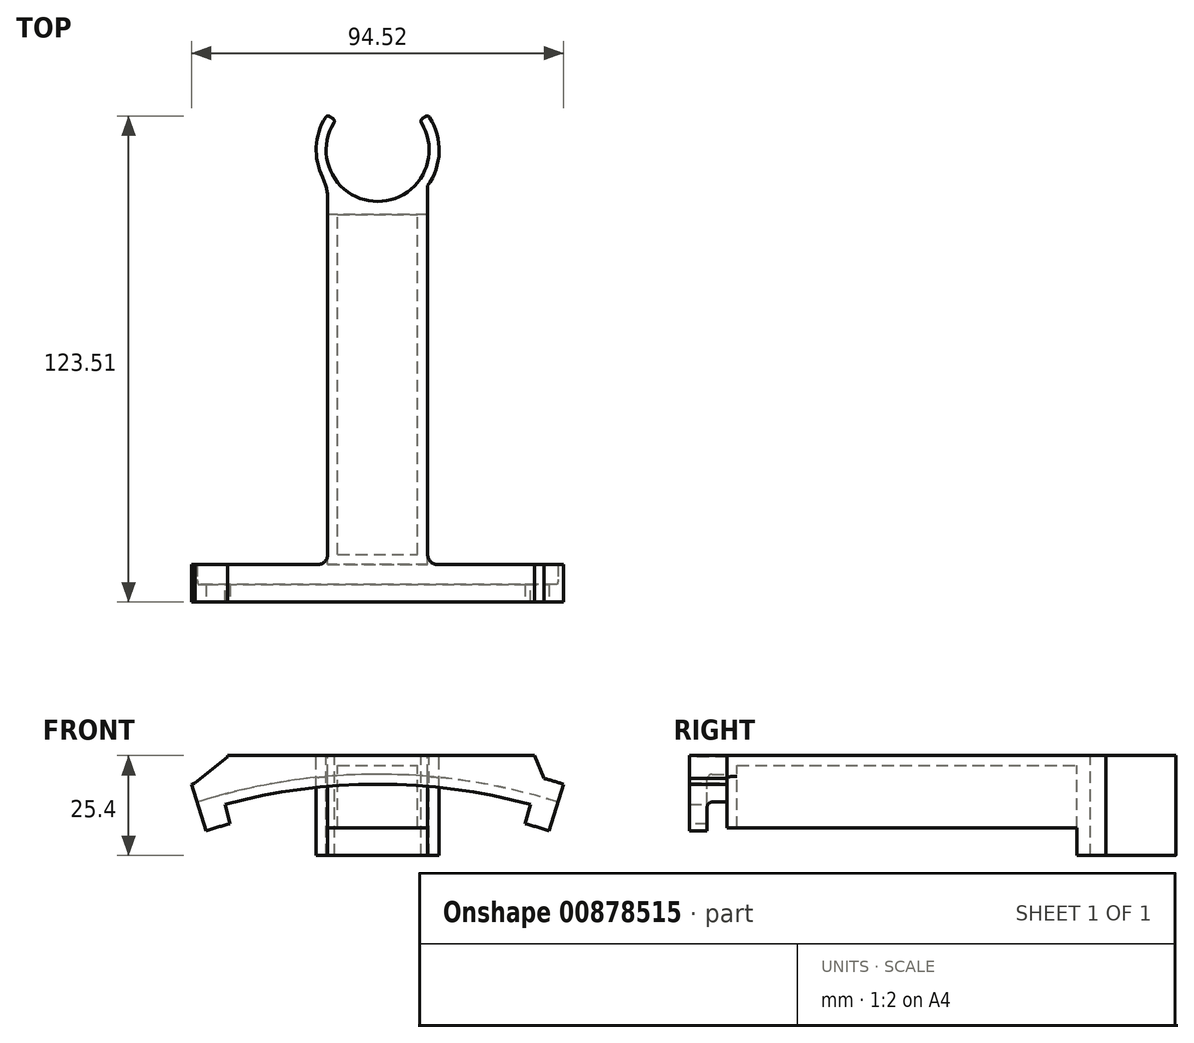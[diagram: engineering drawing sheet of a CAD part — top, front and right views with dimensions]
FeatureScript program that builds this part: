
annotation { "Feature Type Name" : "Feature", "Feature Type Description" : "" }
export const myFeature = defineFeature(function(context is Context, id is Id, definition is map)
    precondition{}
    {
        {
            var Q0;
            Q0=qCreatedBy(makeId("Top.planeOp"),FACE);
            var sketch = newSketch(context, id + "F0", { "sketchPlane" : qUnion([Q0])});
            skCircle(sketch, "E0", {"center": v(0, 0) * mm, "radius": 15.62 * mm});
            skCircle(sketch, "E1", {"center": v(0, 0) * mm, "radius": 13.08 * mm});
            skLineSegment(sketch, "E2", {"start": v(-53.94, 0) * mm, "end": v(51.47, 0) * mm, "construction": true});
            skLineSegment(sketch, "E3", {"start": v(0, 37.95) * mm, "end": v(0, -48.77) * mm, "construction": true});
            skLineSegment(sketch, "E4", {"start": v(0, 0) * mm, "end": v(-12.8, 8.96) * mm});
            skLineSegment(sketch, "E5.MirrorCS", {"start": v(0, 0) * mm, "end": v(12.8, 8.96) * mm});
            skLineSegment(sketch, "E6.top", {"start": v(-12.7, -16.43) * mm, "end": v(12.7, -16.43) * mm});
            skLineSegment(sketch, "E6.left", {"start": v(-12.7, -9.1) * mm, "end": v(-12.7, -16.43) * mm});
            skLineSegment(sketch, "E6.right", {"start": v(12.7, -9.1) * mm, "end": v(12.7, -16.43) * mm});
            skPoint(sketch, "E6.middle", {"position": v(0, -12.76) * mm});
            skCircle(sketch, "E7", {"center": v(0, 0) * mm, "radius": 13.34 * mm, "construction": true});
            skSolve(sketch);
        }
        {
            var Q0;
            {var subQ0=sQuery(id+"F0.wireOp",EDGE,"E4");var subQ5=sQuery(id+"F0.wireOp",EDGE,"E0");var subQ9=makeQuery(id+"F0.imprint","INTERSECT",VERTEX,{"derivedFrom":[subQ5,subQ0]});Q0=makeQuery(id+"F0.imprint","IMPRINT",FACE,{"disambiguationData":[TD([[makeQuery(id+"F0.imprint","IMPRINT",EDGE,{"disambiguationData":[TD([[subQ9,-1.0]])],"derivedFrom":subQ5}),1.0]])]});}
            extrude(context, id + "F1", {"entities" : qUnion([Q0]), "oppositeDirection" : true, "depth" : 25.4 * mm, "offsetDistance" : 25.4 * mm});
        }
        {
            var Q0;
            Q0=makeQuery(id+"F0.imprint","IMPRINT",FACE,{"disambiguationData":[TD([[makeQuery(id+"F0.imprint","IMPRINT",EDGE,{"derivedFrom":sQuery(id+"F0.wireOp",EDGE,"E6.top")}),1.0]])]});
            var Q1;
            Q1=makeQuery(id+"F1.opExtrude","CAP_FACE",FACE,{"disambiguationData":[OSD([sQuery(id+"F0.wireOp",EDGE,"E0"),sQuery(id+"F0.wireOp",EDGE,"E1"),sQuery(id+"F0.wireOp",EDGE,"E4"),sQuery(id+"F0.wireOp",EDGE,"E5.MirrorCS")])],"isStart":false});
            extrude(context, id + "F2", {"entities" : qUnion([Q0]), "operationType" : NewBodyOperationType.ADD, "endBound" : BoundingType.UP_TO_SURFACE, "oppositeDirection" : true, "depth" : 19.05 * mm, "endBoundEntityFace" : qUnion([Q1]), "offsetDistance" : 25.4 * mm});
        }
        {
            var Q0;
            Q0=makeQuery(id+"F2.opExtrude","SWEPT_EDGE",EDGE,{"disambiguationData":[OSD([sQuery(id+"F0.wireOp",EDGE,"E0"),sQuery(id+"F0.wireOp",EDGE,"E6.left")])]});
            var Q1;
            Q1=makeQuery(id+"F2.opExtrude","SWEPT_EDGE",EDGE,{"disambiguationData":[OSD([sQuery(id+"F0.wireOp",EDGE,"E0"),sQuery(id+"F0.wireOp",EDGE,"E6.right")])]});
            fillet(context, id + "F3", {"entities" : qUnion([Q0, Q1]), "radius" : 12.7 * mm, "tangentPropagation" : true, "allowEdgeOverflow" : false});
        }
        {
            var Q0;
            Q0=makeQuery(id+"F1.opExtrude","SWEPT_EDGE",EDGE,{"disambiguationData":[OSD([sQuery(id+"F0.wireOp",EDGE,"E0"),sQuery(id+"F0.wireOp",EDGE,"E4")])]});
            var Q1;
            Q1=makeQuery(id+"F1.opExtrude","SWEPT_EDGE",EDGE,{"disambiguationData":[OSD([sQuery(id+"F0.wireOp",EDGE,"E1"),sQuery(id+"F0.wireOp",EDGE,"E4")])]});
            var Q2;
            Q2=makeQuery(id+"F1.opExtrude","SWEPT_EDGE",EDGE,{"disambiguationData":[OSD([sQuery(id+"F0.wireOp",EDGE,"E0"),sQuery(id+"F0.wireOp",EDGE,"E5.MirrorCS")])]});
            var Q3;
            Q3=makeQuery(id+"F1.opExtrude","SWEPT_EDGE",EDGE,{"disambiguationData":[OSD([sQuery(id+"F0.wireOp",EDGE,"E1"),sQuery(id+"F0.wireOp",EDGE,"E5.MirrorCS")])]});
            fillet(context, id + "F4", {"entities" : qUnion([Q0, Q1, Q2, Q3]), "radius" : 0.76 * mm, "tangentPropagation" : true, "allowEdgeOverflow" : false});
        }
        {
            var Q0;
            Q0=makeQuery(id+"F2.opExtrude","SWEPT_FACE",FACE,{"disambiguationData":[OSD([sQuery(id+"F0.wireOp",EDGE,"E6.top")])]});
            var sketch = newSketch(context, id + "F5", { "sketchPlane" : qUnion([Q0])});
            skLineSegment(sketch, "E8.0", {"start": v(12.7, -25.4) * mm, "end": v(12.7, 0) * mm});
            skLineSegment(sketch, "E8.1", {"start": v(-12.7, 0) * mm, "end": v(12.7, 0) * mm});
            skLineSegment(sketch, "E8.2", {"start": v(-12.7, -25.4) * mm, "end": v(-12.7, 0) * mm});
            skLineSegment(sketch, "E9.0", {"start": v(-10.16, -25.4) * mm, "end": v(-10.16, -2.54) * mm});
            skLineSegment(sketch, "E9.1", {"start": v(-10.16, -2.54) * mm, "end": v(10.16, -2.54) * mm});
            skLineSegment(sketch, "E9.2", {"start": v(10.16, -25.4) * mm, "end": v(10.16, -2.54) * mm});
            skLineSegment(sketch, "E10", {"start": v(12.7, -18.41) * mm, "end": v(-12.7, -18.41) * mm});
            skSolve(sketch);
        }
        {
            var Q0;
            {var subQ1=sQuery(id+"F5.wireOp",EDGE,"E8.1");Q0=makeQuery(id+"F5.imprint","IMPRINT",FACE,{"disambiguationData":[TD([[makeQuery(id+"F5.imprint","IMPRINT",EDGE,{"derivedFrom":subQ1}),-1.0]])]});}
            extrude(context, id + "F6", {"entities" : qUnion([Q0]), "operationType" : NewBodyOperationType.ADD, "depth" : 88.9 * mm, "offsetDistance" : 25.4 * mm});
        }
        {
            var Q0;
            Q0=makeQuery(id+"F6.opExtrude","CAP_FACE",FACE,{"disambiguationData":[OSD([sQuery(id+"F5.wireOp",EDGE,"E8.0"),sQuery(id+"F5.wireOp",EDGE,"E8.1"),sQuery(id+"F5.wireOp",EDGE,"E8.2"),sQuery(id+"F5.wireOp",EDGE,"E9.0"),sQuery(id+"F5.wireOp",EDGE,"E9.1"),sQuery(id+"F5.wireOp",EDGE,"E9.2"),sQuery(id+"F5.wireOp",EDGE,"E10")])],"isStart":false});
            var sketch = newSketch(context, id + "F7", { "sketchPlane" : qUnion([Q0])});
            skLineSegment(sketch, "E11.bottom", {"start": v(12.7, 0) * mm, "end": v(-12.7, 0) * mm});
            skLineSegment(sketch, "E11.top", {"start": v(12.7, -18.41) * mm, "end": v(-12.7, -18.41) * mm});
            skLineSegment(sketch, "E11.left", {"start": v(12.7, 0) * mm, "end": v(12.7, -18.41) * mm});
            skLineSegment(sketch, "E11.right", {"start": v(-12.7, 0) * mm, "end": v(-12.7, -18.41) * mm});
            skSolve(sketch);
        }
        {
            var Q0;
            Q0 = qSketchRegion(id + "F7", true);
            extrude(context, id + "F8", {"entities" : qUnion([Q0]), "operationType" : NewBodyOperationType.ADD, "oppositeDirection" : true, "depth" : 2.54 * mm, "offsetDistance" : 25.4 * mm});
        }
        {
            var Q0;
            Q0=makeQuery(id+"F6.opExtrude","CAP_FACE",FACE,{"disambiguationData":[OSD([sQuery(id+"F5.wireOp",EDGE,"E8.0"),sQuery(id+"F5.wireOp",EDGE,"E8.1"),sQuery(id+"F5.wireOp",EDGE,"E8.2"),sQuery(id+"F5.wireOp",EDGE,"E9.0"),sQuery(id+"F5.wireOp",EDGE,"E9.1"),sQuery(id+"F5.wireOp",EDGE,"E9.2"),sQuery(id+"F5.wireOp",EDGE,"CikZGe1Q-anNP-ZjDr-t5UD-7ZgGB5lJed3H"),sQuery(id+"F5.wireOp",EDGE,"0FJpHfQZ-AEC0-XV2y-uZry-Wgd810QdxFEr")])],"isStart":false});
            var sketch = newSketch(context, id + "F9", { "sketchPlane" : qUnion([Q0])});
            skLineSegment(sketch, "E12", {"start": v(0, 225.36) * mm, "end": v(0, -360.44) * mm, "construction": true});
            skCircle(sketch, "E13", {"center": v(0, -157.16) * mm, "radius": 152.4 * mm});
            skLineSegment(sketch, "E14", {"start": v(40.16, -4.76) * mm, "end": v(-54.87, -4.76) * mm, "construction": true});
            skSolve(sketch);
        }
        {
            var Q0;
            Q0=qCreatedBy(makeId("Right.planeOp"),FACE);
            var sketch = newSketch(context, id + "F10", { "sketchPlane" : qUnion([Q0])});
            skLineSegment(sketch, "E15", {"start": v(-114.86, 0) * mm, "end": v(-105.33, 0) * mm});
            skLineSegment(sketch, "E16", {"start": v(-105.33, 0) * mm, "end": v(-105.33, -4.76) * mm});
            skLineSegment(sketch, "E17", {"start": v(-105.33, -4.76) * mm, "end": v(-110.41, -4.76) * mm});
            skLineSegment(sketch, "E18", {"start": v(-110.41, -4.76) * mm, "end": v(-110.41, -12.38) * mm});
            skLineSegment(sketch, "E19", {"start": v(-110.41, -12.38) * mm, "end": v(-114.86, -12.38) * mm});
            skLineSegment(sketch, "E20", {"start": v(-114.86, -12.38) * mm, "end": v(-114.86, 0) * mm});
            skLineSegment(sketch, "E21.top", {"start": v(-114.86, -3.81) * mm, "end": v(-105.33, -3.81) * mm});
            skLineSegment(sketch, "E21.left", {"start": v(-114.86, 0) * mm, "end": v(-114.86, -3.81) * mm});
            skLineSegment(sketch, "E21.right", {"start": v(-105.33, 0) * mm, "end": v(-105.33, -3.81) * mm});
            skLineSegment(sketch, "E22.bottom", {"start": v(-114.86, -12.38) * mm, "end": v(-110.41, -12.38) * mm});
            skLineSegment(sketch, "E22.top", {"start": v(-114.86, -7.3) * mm, "end": v(-110.41, -7.3) * mm});
            skLineSegment(sketch, "E22.left", {"start": v(-114.86, -12.38) * mm, "end": v(-114.86, -7.3) * mm});
            skLineSegment(sketch, "E22.right", {"start": v(-110.41, -12.38) * mm, "end": v(-110.41, -7.3) * mm});
            skSolve(sketch);
        }
        {
            var Q0;
            Q0=qSketchRegion(id+"F10",true);
            var Q1;
            Q1=sQuery(id+"F9.wireOp",EDGE,"E13");
            revolve(context, id + "F11", {"operationType" : NewBodyOperationType.ADD, "surfaceOperationType" : NewSurfaceOperationType.NEW, "entities" : qUnion([Q0]), "axis" : qUnion([Q1]), "revolveType" : RevolveType.SYMMETRIC, "angle" : 35 * degree});
        }
        {
            var Q0;
            Q0=makeQuery(id+"F11.opRevolve","SWEPT_EDGE",EDGE,{"disambiguationData":[OSD([sQuery(id+"F10.wireOp",EDGE,"E17"),sQuery(id+"F10.wireOp",EDGE,"E18")])]});
            fillet(context, id + "F12", {"entities" : qUnion([Q0]), "tangentPropagation" : true, "radius" : 1.27 * mm, "defaultsChanged" : true, "vertexSettings" : [], "allowEdgeOverflow" : false});
        }
        {
            var Q0;
            Q0=qSketchRegion(id+"F10",true);
            extrude(context, id + "F13", {"entities" : qUnion([Q0]), "operationType" : NewBodyOperationType.ADD, "endBound" : BoundingType.SYMMETRIC, "depth" : 76.2 * mm, "offsetDistance" : 25.4 * mm});
        }
        {
            var Q0;
            {var subQ0=sQuery(id+"F0.wireOp",EDGE,"E6.left");var subQ1=makeQuery(id+"F2.opExtrude","SWEPT_FACE",FACE,{"disambiguationData":[OSD([subQ0])]});var subQ2=makeQuery(id+"F11.opRevolve","SWEPT_FACE",FACE,{"disambiguationData":[OSD([sQuery(id+"F10.wireOp",EDGE,"E16")])]});var subQ3=sQuery(id+"F5.wireOp",EDGE,"E8.2");var subQ4=makeQuery(id+"F6.opExtrude","SWEPT_FACE",FACE,{"disambiguationData":[OSD([subQ3])]});var subQ5=makeQuery(id+"F6.opExtrude","CAP_EDGE",EDGE,{"disambiguationData":[OSD([subQ3])],"isStart":false});var subQ6=sQuery(id+"F5.wireOp",EDGE,"E8.1");var subQ7=makeQuery(id+"F6.opExtrude","CAP_FACE",FACE,{"disambiguationData":[OSD([sQuery(id+"F5.wireOp",EDGE,"E8.0"),subQ6,subQ3,sQuery(id+"F5.wireOp",EDGE,"E9.0"),sQuery(id+"F5.wireOp",EDGE,"E9.1"),sQuery(id+"F5.wireOp",EDGE,"E9.2"),sQuery(id+"F5.wireOp",EDGE,"E10")])],"isStart":false});var subQ9=makeQuery(id+"F8.opExtrude","CAP_FACE",FACE,{"disambiguationData":[OSD([sQuery(id+"F7.wireOp",EDGE,"E11.bottom"),sQuery(id+"F7.wireOp",EDGE,"E11.top"),sQuery(id+"F7.wireOp",EDGE,"E11.left"),sQuery(id+"F7.wireOp",EDGE,"E11.right")])],"isStart":true});Q0=makeQuery(id+"F13.boolean.opBoolean","MERGE",EDGE,{"derivedFrom":[makeQuery(id+"F11.boolean.opBoolean","SPLIT",EDGE,{"disambiguationData":[topologyDisambiguationEdgeConnected([subQ1,subQ7,subQ4,subQ9]),TD([makeQuery(id+"F6.opExtrude","SWEPT_FACE",FACE,{"disambiguationData":[OSD([subQ6])]})])],"derivedFrom":subQ5}),makeQuery(id+"F11.boolean.opBoolean","SPLIT",EDGE,{"disambiguationData":[topologyDisambiguationEdgeConnected([subQ1,subQ4,subQ2])],"derivedFrom":subQ5})]});}
            var Q1;
            {var subQ0=sQuery(id+"F0.wireOp",EDGE,"E6.right");var subQ1=makeQuery(id+"F2.opExtrude","SWEPT_FACE",FACE,{"disambiguationData":[OSD([subQ0])]});var subQ2=sQuery(id+"F5.wireOp",EDGE,"E8.0");var subQ3=makeQuery(id+"F6.opExtrude","SWEPT_FACE",FACE,{"disambiguationData":[OSD([subQ2])]});var subQ4=makeQuery(id+"F11.opRevolve","SWEPT_FACE",FACE,{"disambiguationData":[OSD([sQuery(id+"F10.wireOp",EDGE,"E16")])]});var subQ5=makeQuery(id+"F6.opExtrude","CAP_EDGE",EDGE,{"disambiguationData":[OSD([subQ2])],"isStart":false});var subQ7=sQuery(id+"F5.wireOp",EDGE,"E8.1");var subQ8=makeQuery(id+"F8.opExtrude","CAP_FACE",FACE,{"disambiguationData":[OSD([sQuery(id+"F7.wireOp",EDGE,"E11.bottom"),sQuery(id+"F7.wireOp",EDGE,"E11.top"),sQuery(id+"F7.wireOp",EDGE,"E11.left"),sQuery(id+"F7.wireOp",EDGE,"E11.right")])],"isStart":true});var subQ9=makeQuery(id+"F6.opExtrude","CAP_FACE",FACE,{"disambiguationData":[OSD([subQ2,subQ7,sQuery(id+"F5.wireOp",EDGE,"E8.2"),sQuery(id+"F5.wireOp",EDGE,"E9.0"),sQuery(id+"F5.wireOp",EDGE,"E9.1"),sQuery(id+"F5.wireOp",EDGE,"E9.2"),sQuery(id+"F5.wireOp",EDGE,"E10")])],"isStart":false});Q1=makeQuery(id+"F13.boolean.opBoolean","MERGE",EDGE,{"derivedFrom":[makeQuery(id+"F11.boolean.opBoolean","SPLIT",EDGE,{"disambiguationData":[topologyDisambiguationEdgeConnected([subQ1,subQ3,subQ9,subQ8]),TD([makeQuery(id+"F6.opExtrude","SWEPT_FACE",FACE,{"disambiguationData":[OSD([subQ7])]})])],"derivedFrom":subQ5}),makeQuery(id+"F11.boolean.opBoolean","SPLIT",EDGE,{"disambiguationData":[topologyDisambiguationEdgeConnected([subQ1,subQ3,subQ4])],"derivedFrom":subQ5})]});}
            fillet(context, id + "F14", {"entities" : qUnion([Q0, Q1]), "tangentPropagation" : true, "radius" : 2.54 * mm, "defaultsChanged" : false, "vertexSettings" : [], "allowEdgeOverflow" : false});
        }
        {
            var Q0;
            {var subQ2=sQuery(id+"F10.wireOp",EDGE,"E19");Q0=makeQuery(id+"F10.imprint","IMPRINT",FACE,{"disambiguationData":[TD([[makeQuery(id+"F10.imprint","IMPRINT",EDGE,{"derivedFrom":subQ2}),-1.0]])]});}
            var Q1;
            Q1=makeQuery(id+"F11.opRevolve","SWEPT_EDGE",EDGE,{"disambiguationData":[OSD([sQuery(id+"F10.wireOp",EDGE,"E19"),sQuery(id+"F10.wireOp",EDGE,"E20")])]});
            revolve(context, id + "F15", {"operationType" : NewBodyOperationType.REMOVE, "surfaceOperationType" : NewSurfaceOperationType.NEW, "entities" : qUnion([Q0]), "axis" : qUnion([Q1]), "revolveType" : RevolveType.SYMMETRIC, "oppositeDirection" : true, "angle" : 30 * degree});
        }
        {
            var Q0;
            {var subQ0=sQuery(id+"F10.wireOp",EDGE,"E15");Q0=makeQuery(id+"F13.boolean.opBoolean","INTERSECT",EDGE,{"derivedFrom":[makeQuery(id+"F11.opRevolve","SWEPT_FACE",FACE,{"disambiguationData":[OSD([subQ0])]}),makeQuery(id+"F13.opExtrude","CAP_FACE",FACE,{"disambiguationData":[OSD([subQ0,sQuery(id+"F10.wireOp",EDGE,"E16"),sQuery(id+"F10.wireOp",EDGE,"E17"),sQuery(id+"F10.wireOp",EDGE,"E18"),sQuery(id+"F10.wireOp",EDGE,"E19"),sQuery(id+"F10.wireOp",EDGE,"E20")])],"isStart":false})]});}
            var Q1;
            {var subQ0=sQuery(id+"F10.wireOp",EDGE,"E15");Q1=makeQuery(id+"F13.boolean.opBoolean","INTERSECT",EDGE,{"derivedFrom":[makeQuery(id+"F11.opRevolve","SWEPT_FACE",FACE,{"disambiguationData":[OSD([subQ0])]}),makeQuery(id+"F13.opExtrude","CAP_FACE",FACE,{"disambiguationData":[OSD([subQ0,sQuery(id+"F10.wireOp",EDGE,"E16"),sQuery(id+"F10.wireOp",EDGE,"E17"),sQuery(id+"F10.wireOp",EDGE,"E18"),sQuery(id+"F10.wireOp",EDGE,"E19"),sQuery(id+"F10.wireOp",EDGE,"E20")])],"isStart":true})]});}
            chamfer(context, id + "F16", {"entities" : qUnion([Q0, Q1]), "chamferType" : ChamferType.TWO_OFFSETS, "width1" : 4.57 * mm, "oppositeDirection" : false, "width2" : 8.9 * mm, "tangentPropagation" : true});
        }
    });
